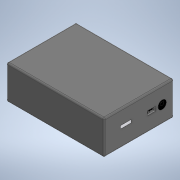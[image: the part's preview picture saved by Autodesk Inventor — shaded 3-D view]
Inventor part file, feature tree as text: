
AUTODESK INVENTOR PART (.ipt)
format: ipt  version: 2021 (Build 250183000, 183)  size: 199,168 bytes
history: native  units: mm
features: extrude x8, sketch x4, fillet x3, projected_geometry x1
ambient origin geometry x8: Origin, YZ Plane, XZ Plane, XY Plane, X Axis, Y Axis, Z Axis, Center Point
bodies: Solid1 (feature_tree)
feature tree (16):
  extrude  "Extrusion1"  Depth=115.0mm
  fillet  "Fillet1"  Radius=56.0mm
  sketch  "Sketch2"  dims[d4=2.5mm d5=26.0mm]
  extrude  "Extrusion2"  Depth=26.0mm
  extrude  "Extrusion3"  Depth=14.0mm
  extrude  "Extrusion4"  Depth=30.0mm
  extrude  "Extrusion5"  Depth=17.5mm
  extrude  "Extrusion7"  Depth=5.0mm
  extrude  "Extrusion8"  Depth=70.0mm
  fillet  "Fillet2"  Radius=23.5mm
  extrude  "Extrusion9"  Depth=24.5mm
  fillet  "Fillet3"  Radius=4.0mm
  sketch  "Sketch1"  dims[d0=161.0mm d1=115.0mm d2=56.0mm d3=0.0mm]
  projected_geometry  "Projected Loop1"
  sketch  "Sketch3"  dims[d6=19.0mm d7=14.0mm]
  sketch  "Sketch4"  dims[d8=7.0mm d9=30.0mm d10=17.5mm d11=5.0mm d12=70.0mm d13=23.5mm d14=24.5mm d15=4.0mm d16=33.0mm d17=41.0mm d18=6.0mm d19=6.0mm d20=14.0mm d21=19.0mm d22=6.0mm d23=10.0mm d24=0.0mm d25=0.1mm d26=0.0mm d27=10.0mm d28=0.0mm d29=5.0mm d30=0.0mm d33=0.2mm d34=0.0mm d35=2.5mm d36=8.0mm d37=0.0mm d38=1.25mm d39=2.8mm d40=1.8mm d41=5.0mm d42=0.0mm d43=0.25mm d44=28.0mm d45=28.0mm d46=28.0mm]
